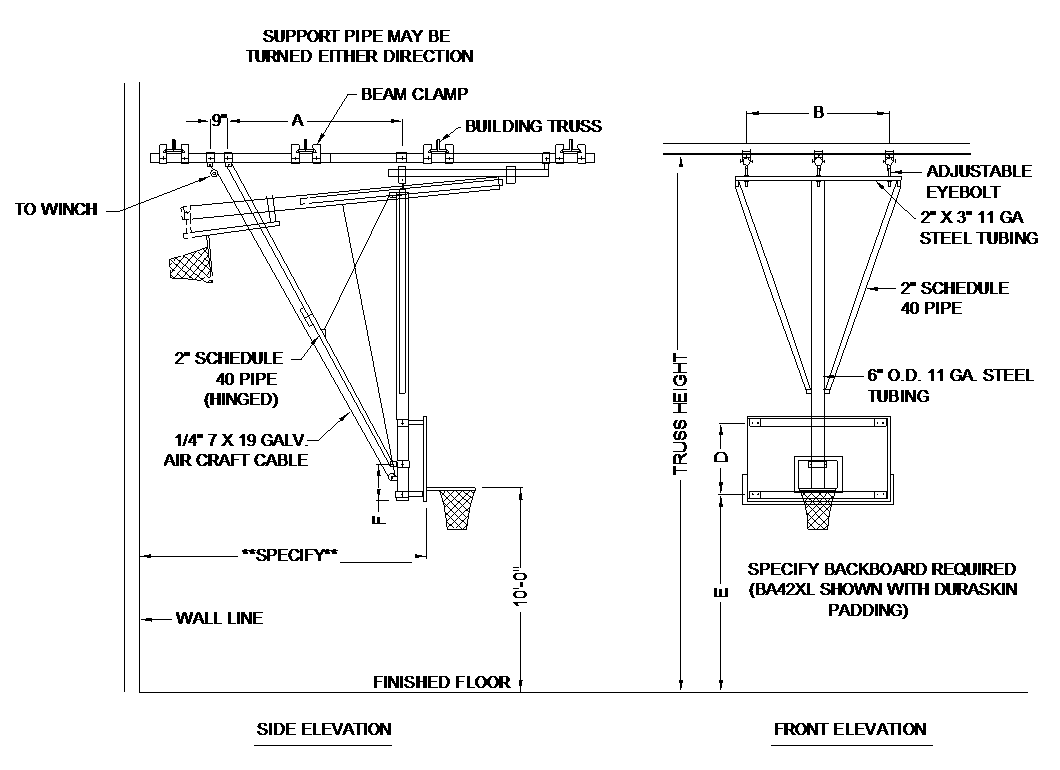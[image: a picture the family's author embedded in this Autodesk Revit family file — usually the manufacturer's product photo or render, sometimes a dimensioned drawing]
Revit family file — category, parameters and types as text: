
# Revit family: Basketball_Backstop-Ceiling_Mount-Forward_Roll_Backward_Fold-IPIbyBison-IP1345FRBF
name_source: partatom
category: Specialty Equipment
units: mm (PartAtom-declared; Revit-internal decimal feet)

## family parameters
Always vertical = Yes
Cut with Voids When Loaded = No
Maintain Annotation Orientation = No
OmniClass Number = 23.40.50.34.14
OmniClass Title = Gymnasium Equipment
Part Type = Normal
Room Calculation Point = No
Round Connector Dimension = Use Diameter
Shared = No

## types (1)
- Forward Rolling/Back Folding Ceiling Braced
    Assembly Code = E1090
    Available Options = as Specified
    Backboard Type = Backboard_BA42XLGlass
    CAD Details = https://www.arcat.com
    Default Elevation = 0' - 0"
    Description = Back Folding Basketball Frame and Backboard, Ceiling Mount
    Keynote = 11 66 00
    Manufacturer = IPI by Bison
    Model = IP1345FRBF
    Product Page URL = https://www.arcat.com
    Specification = https://www.arcat.com
    URL = https://ipibybison.com

## geometry (parser evidence)
native form markers: Sweep x7
no freeform markers — native parametric forms only
